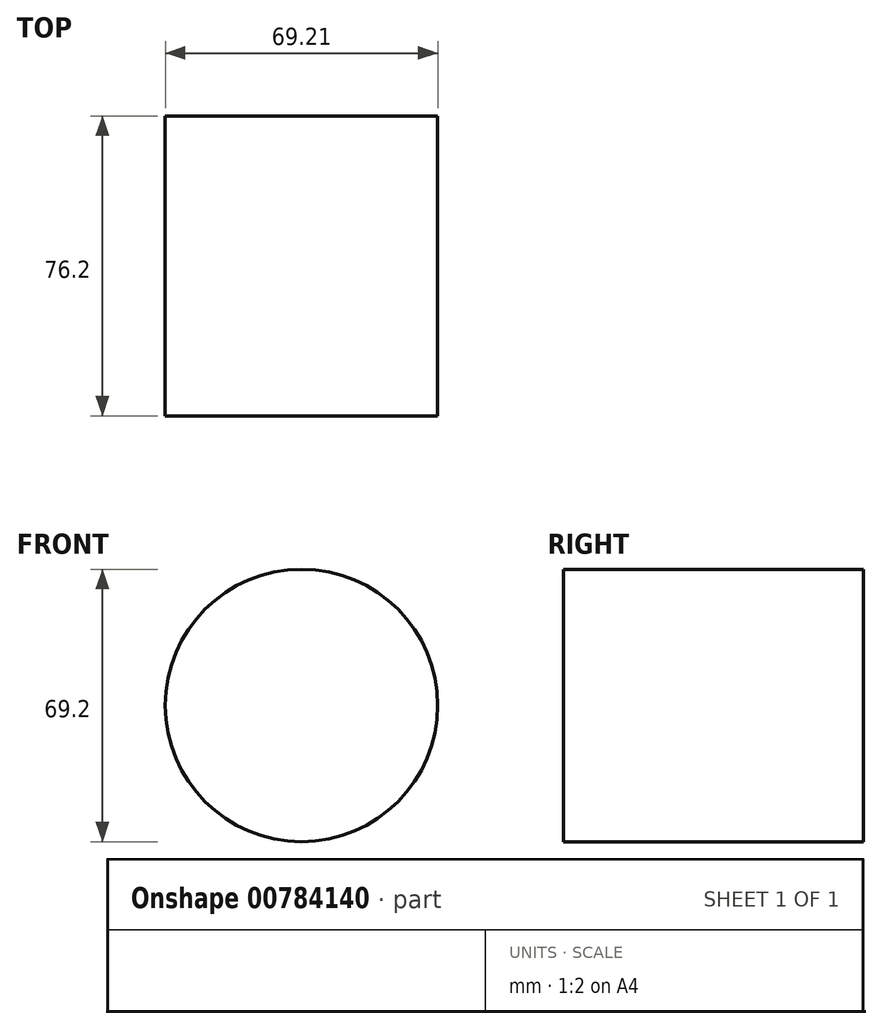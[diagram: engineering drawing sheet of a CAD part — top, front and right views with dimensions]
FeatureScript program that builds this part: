
annotation { "Feature Type Name" : "Feature", "Feature Type Description" : "" }
export const myFeature = defineFeature(function(context is Context, id is Id, definition is map)
    precondition{}
    {
        {
            var Q0;
            Q0=qCreatedBy(makeId("Front.planeOp"),FACE);
            var sketch = newSketch(context, id + "F0", { "sketchPlane" : qUnion([Q0])});
            skCircle(sketch, "E0", {"center": v(15.37, 10.98) * mm, "radius": 34.6 * mm});
            skSolve(sketch);
        }
        {
            var Q0;
            Q0=makeQuery(id+"F0.imprint","IMPRINT",FACE,{"disambiguationData":[TD([[makeQuery(id+"F0.imprint","IMPRINT",EDGE,{"derivedFrom":sQuery(id+"F0.wireOp",EDGE,"E0")}),1.0]])]});
            extrude(context, id + "F1", {"entities" : qUnion([Q0]), "depth" : 76.2 * mm, "offsetDistance" : 25.4 * mm});
        }
    });
